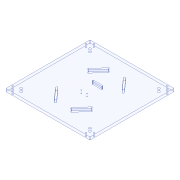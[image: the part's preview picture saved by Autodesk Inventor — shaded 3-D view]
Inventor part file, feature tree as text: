
AUTODESK INVENTOR PART (.ipt)
format: ipt  version: 2020 (Build 240168000, 168)  size: 260,096 bytes
history: native  units: mm
features: extrude x10, sketch x10, plane x1, mirror x1, fillet x1, other x1
ambient origin geometry x8: Origin, YZ Plane, XZ Plane, XY Plane, X Axis, Y Axis, Z Axis, Center Point
bodies: Solid1 (feature_tree)
feature tree (24):
  extrude  "Extrusion1"  Depth=8.1mm
  extrude  "Extrusion2"  Depth=8.1mm
  extrude  "Extrusion3"  Depth=6.0mm
  plane  "Work Plane1"
  mirror  "Mirror1"
  extrude  "Extrusion4"  Depth=55.0mm
  extrude  "Extrusion5"  Depth=55.0mm
  extrude  "Extrusion6"  Depth=6.0mm
  extrude  "Extrusion8"  Depth=6.0mm
  extrude  "Extrusion7"  Depth=50.0mm
  extrude  "Extrusion9"  Depth=10.0mm TaperAngle=0.0deg
  extrude  "Extrusion10"  Depth=5.0mm
  fillet  "Fillet1"  Radius=100.0mm
  sketch  "Sketch1"  dims[d0=8.1mm d1=8.1mm]
  sketch  "Sketch2"  dims[d2=8.1mm d3=8.1mm]
  sketch  "Sketch3"  dims[d4=10.0mm d5=0.0mm d6=6.0mm]
  sketch  "Sketch4"  dims[d7=120.0mm d8=55.0mm]
  sketch  "Sketch5"  dims[d9=120.0mm d10=55.0mm]
  sketch  "Sketch7"  dims[d11=6.0mm d12=148.5mm]
  sketch  "Sketch9"  dims[d13=10.0mm d14=0.0mm d15=6.0mm]
  sketch  "Sketch10"  dims[d16=8.5mm d17=50.0mm]
  sketch  "Sketch11"  dims[d18=10.0mm d19=0.0mm d20=10.0mm d21=0.0mm]
  sketch  "Sketch12"  dims[d22=10.0mm d23=5.0mm d24=100.0mm d25=10.0mm d26=0.0mm d27=21.105mm d28=8.1mm d29=10.0mm d30=10.0mm d31=0.0mm d32=20.0mm d33=3.0mm d34=3.0mm d36=10.0mm d37=0.0mm d38=10.0mm d39=0.0mm d40=10.0mm d41=19.0mm d42=25.0mm d43=5.0mm d44=35.0mm d45=10.0mm d46=0.0mm d47=10.0mm d48=0.0mm d49=2.0mm]
  other  "Cut-Extrude14"
